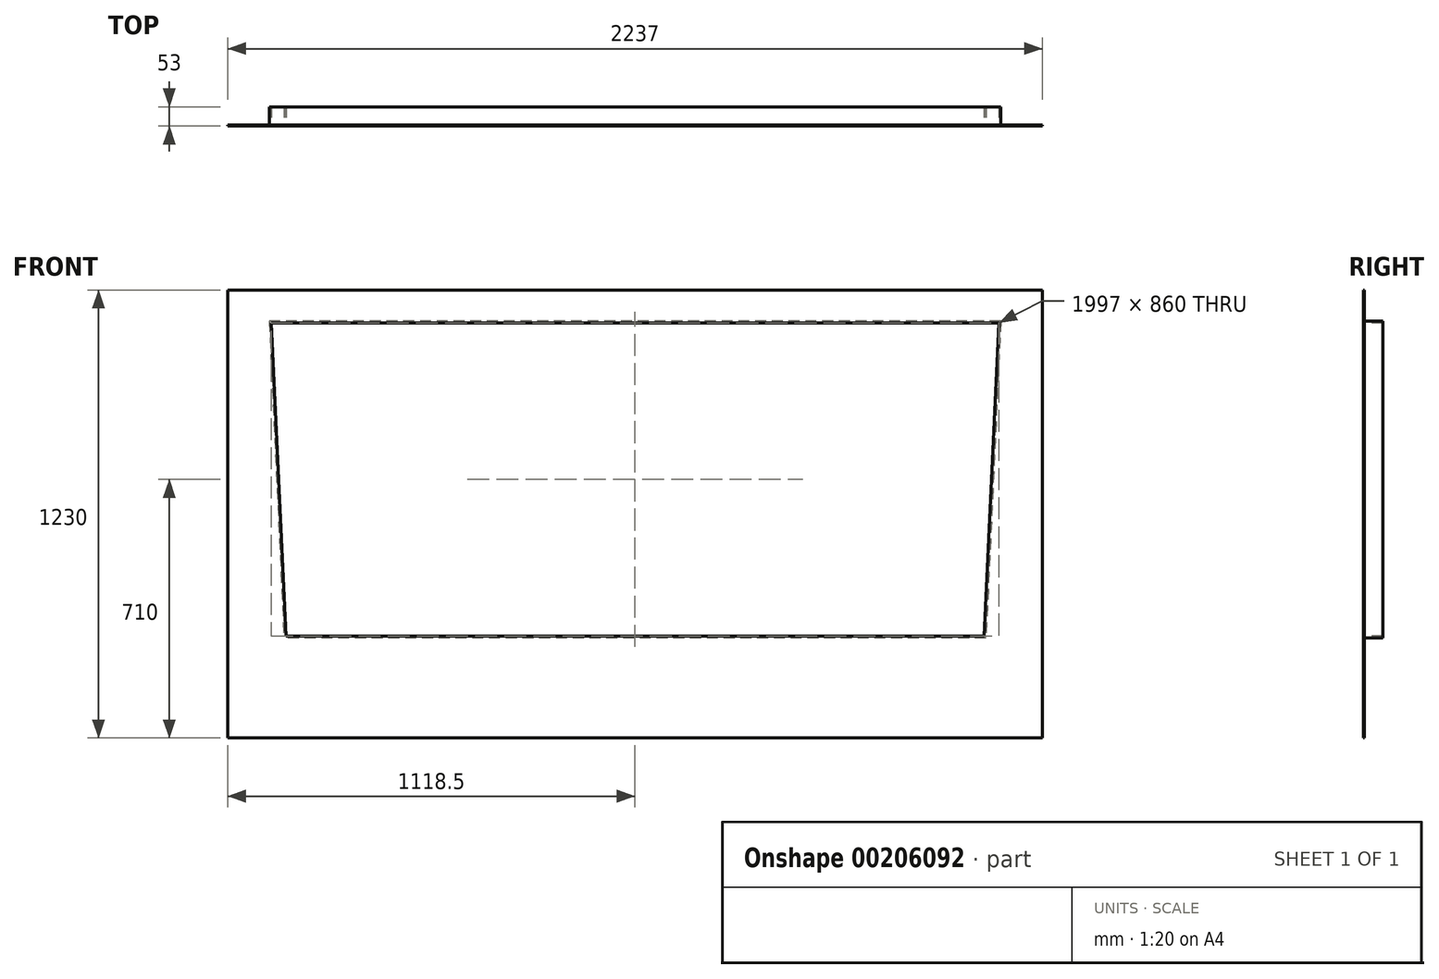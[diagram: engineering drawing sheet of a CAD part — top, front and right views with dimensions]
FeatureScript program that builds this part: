
annotation { "Feature Type Name" : "Feature", "Feature Type Description" : "" }
export const myFeature = defineFeature(function(context is Context, id is Id, definition is map)
    precondition{}
    {
        {
            var Q0;
            Q0=qCreatedBy(makeId("Front.planeOp"),FACE);
            var sketch = newSketch(context, id + "F0", { "sketchPlane" : qUnion([Q0])});
            skLineSegment(sketch, "E0.bottom", {"start": v(1118.5, -615) * mm, "end": v(-1118.5, -615) * mm});
            skLineSegment(sketch, "E0.top", {"start": v(1118.5, 615) * mm, "end": v(-1118.5, 615) * mm});
            skLineSegment(sketch, "E0.left", {"start": v(1118.5, -615) * mm, "end": v(1118.5, 615) * mm});
            skLineSegment(sketch, "E0.right", {"start": v(-1118.5, -615) * mm, "end": v(-1118.5, 615) * mm});
            skPoint(sketch, "E0.middle", {"position": v(0, 0) * mm});
            skSolve(sketch);
        }
        {
            var Q0;
            Q0 = qSketchRegion(id + "F0", true);
            extrude(context, id + "F1", {"entities" : qUnion([Q0]), "depth" : 3 * mm});
        }
        {
            var Q0;
            Q0=makeQuery(id+"F1.opExtrude","CAP_FACE",FACE,{"disambiguationData":[OSD([sQuery(id+"F0.wireOp",EDGE,"E0.bottom"),sQuery(id+"F0.wireOp",EDGE,"E0.top"),sQuery(id+"F0.wireOp",EDGE,"E0.left"),sQuery(id+"F0.wireOp",EDGE,"E0.right")])],"isStart":false});
            var sketch = newSketch(context, id + "F2", { "sketchPlane" : qUnion([Q0])});
            skLineSegment(sketch, "E1", {"start": v(0, 615) * mm, "end": v(0, -615) * mm, "construction": true});
            skLineSegment(sketch, "E2.top", {"start": v(998.5, 525) * mm, "end": v(-998.5, 525) * mm});
            skPoint(sketch, "E2.middle", {"position": v(0, 149.96) * mm});
            skLineSegment(sketch, "E3", {"start": v(-998.5, 525) * mm, "end": v(-1118.5, 525) * mm, "construction": true});
            skLineSegment(sketch, "E4", {"start": v(998.5, 525) * mm, "end": v(1118.5, 525) * mm, "construction": true});
            skLineSegment(sketch, "E5", {"start": v(-998.5, 525) * mm, "end": v(-958.5, -335) * mm});
            skLineSegment(sketch, "E6", {"start": v(-958.5, -335) * mm, "end": v(0, -335) * mm});
            skLineSegment(sketch, "E7.MirrorCS", {"start": v(958.5, -335) * mm, "end": v(0, -335) * mm});
            skLineSegment(sketch, "E8.MirrorCS", {"start": v(998.5, 525) * mm, "end": v(958.5, -335) * mm});
            skSolve(sketch);
        }
        {
            var Q0;
            Q0 = qSketchRegion(id + "F2", true);
            extrude(context, id + "F3", {"entities" : qUnion([Q0]), "operationType" : NewBodyOperationType.REMOVE, "endBound" : BoundingType.THROUGH_ALL, "oppositeDirection" : true, "depth" : 25 * mm});
        }
        {
            var Q0;
            Q0=makeQuery(id+"F1.opExtrude","CAP_FACE",FACE,{"disambiguationData":[OSD([sQuery(id+"F0.wireOp",EDGE,"E0.bottom"),sQuery(id+"F0.wireOp",EDGE,"E0.top"),sQuery(id+"F0.wireOp",EDGE,"E0.left"),sQuery(id+"F0.wireOp",EDGE,"E0.right")])],"isStart":true});
            var sketch = newSketch(context, id + "F4", { "sketchPlane" : qUnion([Q0])});
            skLineSegment(sketch, "E9", {"start": v(998.5, 525) * mm, "end": v(958.5, -335) * mm});
            skLineSegment(sketch, "E10", {"start": v(958.5, -335) * mm, "end": v(-958.5, -335) * mm});
            skLineSegment(sketch, "E11", {"start": v(-958.5, -335) * mm, "end": v(-998.5, 525) * mm});
            skLineSegment(sketch, "E12", {"start": v(-998.5, 525) * mm, "end": v(998.5, 525) * mm});
            skLineSegment(sketch, "E13", {"start": v(-1003.74, 530) * mm, "end": v(1003.74, 530) * mm});
            skLineSegment(sketch, "E14", {"start": v(-1003.74, 530) * mm, "end": v(-963.27, -340) * mm});
            skLineSegment(sketch, "E15", {"start": v(-963.27, -340) * mm, "end": v(963.27, -340) * mm});
            skLineSegment(sketch, "E16", {"start": v(1003.74, 530) * mm, "end": v(963.27, -340) * mm});
            skSolve(sketch);
        }
        {
            var Q0;
            Q0 = qSketchRegion(id + "F4", true);
            extrude(context, id + "F5", {"entities" : qUnion([Q0]), "operationType" : NewBodyOperationType.ADD, "depth" : 50 * mm});
        }
    });
